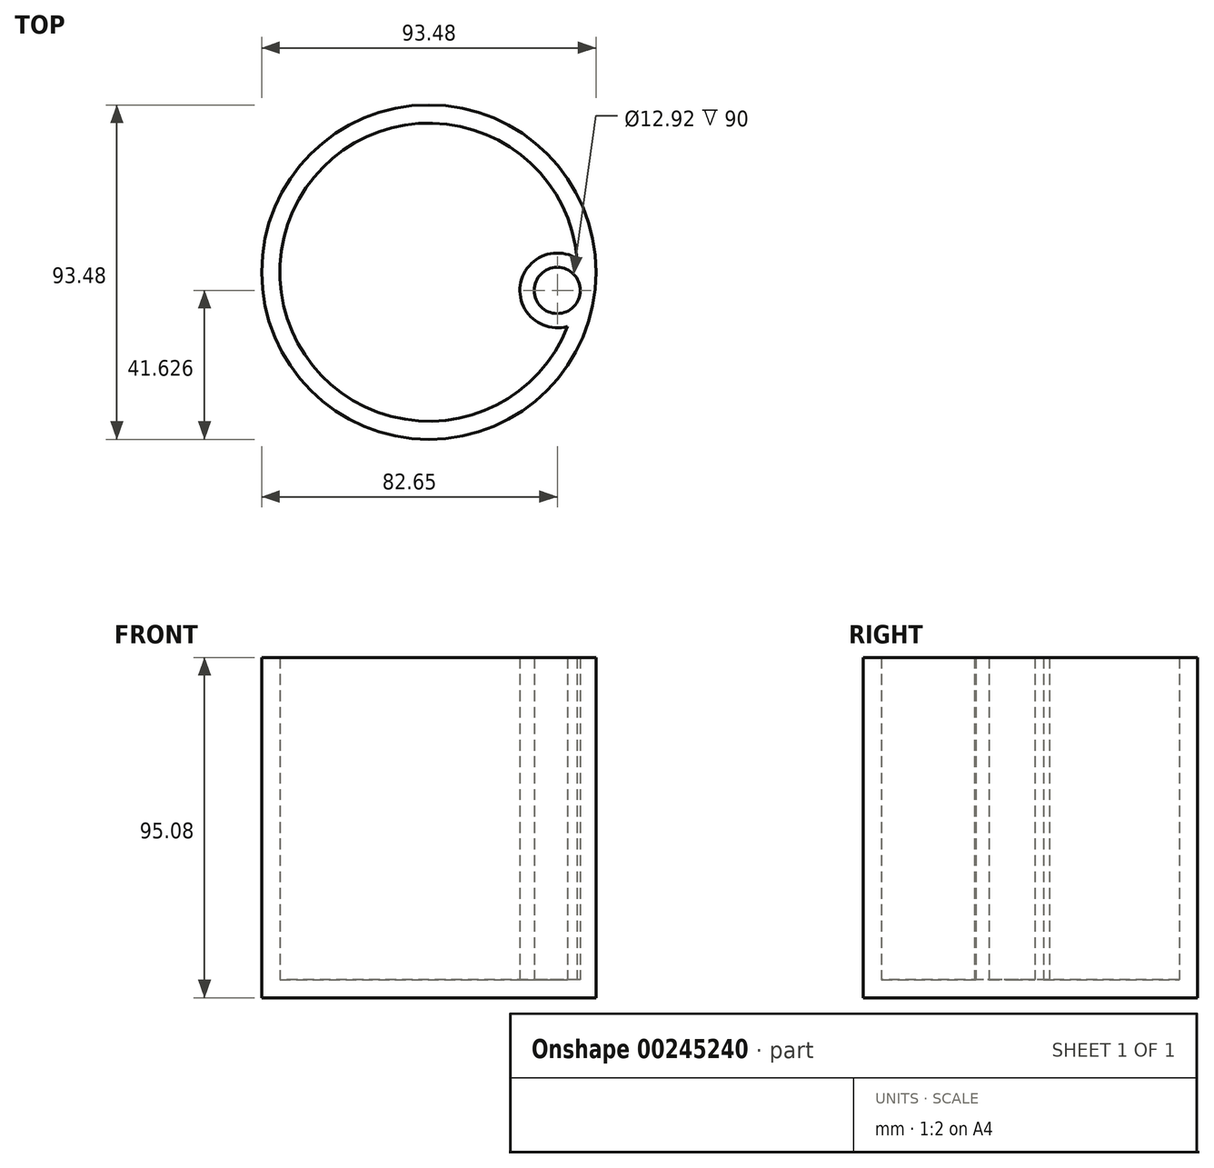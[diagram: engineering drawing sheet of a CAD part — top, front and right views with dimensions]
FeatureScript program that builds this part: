
annotation { "Feature Type Name" : "Feature", "Feature Type Description" : "" }
export const myFeature = defineFeature(function(context is Context, id is Id, definition is map)
    precondition{}
    {
        {
            var Q0;
            Q0=qCreatedBy(makeId("Top.planeOp"),FACE);
            var sketch = newSketch(context, id + "F0", { "sketchPlane" : qUnion([Q0])});
            skCircle(sketch, "E0", {"center": v(0, 0) * mm, "radius": 46.74 * mm});
            skCircle(sketch, "E1", {"center": v(35.9, -5.11) * mm, "radius": 10.46 * mm});
            skCircle(sketch, "E2", {"center": v(35.9, -5.11) * mm, "radius": 6.46 * mm});
            skCircle(sketch, "E3", {"center": v(0, 0) * mm, "radius": 41.66 * mm});
            skSolve(sketch);
        }
        {
            var Q0;
            {var subQ0=sQuery(id+"F0.wireOp",EDGE,"E3");var subQ1=sQuery(id+"F0.wireOp",EDGE,"E1");var subQ2=makeQuery(id+"F0.imprint","INTERSECT",VERTEX,{"disambiguationData":[OD(0.0)],"derivedFrom":[subQ1,subQ0]});Q0=makeQuery(id+"F0.imprint","IMPRINT",FACE,{"disambiguationData":[TD([[makeQuery(id+"F0.imprint","IMPRINT",EDGE,{"disambiguationData":[TD([[subQ2,1.0]])],"derivedFrom":subQ1}),1.0]])]});}
            var Q1;
            {var subQ0=sQuery(id+"F0.wireOp",EDGE,"E3");var subQ1=sQuery(id+"F0.wireOp",EDGE,"E1");var subQ2=makeQuery(id+"F0.imprint","INTERSECT",VERTEX,{"disambiguationData":[OD(0.0)],"derivedFrom":[subQ1,subQ0]});Q1=makeQuery(id+"F0.imprint","IMPRINT",FACE,{"disambiguationData":[TD([[makeQuery(id+"F0.imprint","IMPRINT",EDGE,{"disambiguationData":[TD([[subQ2,-1.0]])],"derivedFrom":subQ1}),1.0]])]});}
            var Q2;
            Q2=makeQuery(id+"F0.imprint","IMPRINT",FACE,{"disambiguationData":[TD([[makeQuery(id+"F0.imprint","IMPRINT",EDGE,{"derivedFrom":sQuery(id+"F0.wireOp",EDGE,"E0")}),1.0]])]});
            extrude(context, id + "F1", {"entities" : qUnion([Q0, Q1, Q2]), "depth" : 90 * mm});
        }
        {
            var Q0;
            Q0 = qSketchRegion(id + "F0", true);
            var Q1;
            {var subQ0=sQuery(id+"F0.wireOp",EDGE,"E3");var subQ1=sQuery(id+"F0.wireOp",EDGE,"E2");var subQ2=makeQuery(id+"F0.imprint","INTERSECT",VERTEX,{"disambiguationData":[OD(0.0)],"derivedFrom":[subQ1,subQ0]});Q1=makeQuery(id+"F0.imprint","IMPRINT",FACE,{"disambiguationData":[TD([[makeQuery(id+"F0.imprint","IMPRINT",EDGE,{"disambiguationData":[TD([[subQ2,1.0]])],"derivedFrom":subQ1}),1.0]])]});}
            var Q2;
            {var subQ0=sQuery(id+"F0.wireOp",EDGE,"E3");var subQ1=sQuery(id+"F0.wireOp",EDGE,"E2");var subQ2=makeQuery(id+"F0.imprint","INTERSECT",VERTEX,{"disambiguationData":[OD(0.0)],"derivedFrom":[subQ1,subQ0]});Q2=makeQuery(id+"F0.imprint","IMPRINT",FACE,{"disambiguationData":[TD([[makeQuery(id+"F0.imprint","IMPRINT",EDGE,{"disambiguationData":[TD([[subQ2,-1.0]])],"derivedFrom":subQ1}),1.0]])]});}
            var Q3;
            {var subQ0=sQuery(id+"F0.wireOp",EDGE,"E3");var subQ1=sQuery(id+"F0.wireOp",EDGE,"E1");var subQ2=makeQuery(id+"F0.imprint","INTERSECT",VERTEX,{"disambiguationData":[OD(0.0)],"derivedFrom":[subQ1,subQ0]});Q3=makeQuery(id+"F0.imprint","IMPRINT",FACE,{"disambiguationData":[TD([[makeQuery(id+"F0.imprint","IMPRINT",EDGE,{"disambiguationData":[TD([[subQ2,1.0]])],"derivedFrom":subQ1}),-1.0]])]});}
            var Q4;
            {var subQ0=sQuery(id+"F0.wireOp",EDGE,"E3");var subQ1=sQuery(id+"F0.wireOp",EDGE,"E1");var subQ2=makeQuery(id+"F0.imprint","INTERSECT",VERTEX,{"disambiguationData":[OD(0.0)],"derivedFrom":[subQ1,subQ0]});Q4=makeQuery(id+"F0.imprint","IMPRINT",FACE,{"disambiguationData":[TD([[makeQuery(id+"F0.imprint","IMPRINT",EDGE,{"disambiguationData":[TD([[subQ2,1.0]])],"derivedFrom":subQ1}),1.0]])]});}
            var Q5;
            {var subQ0=sQuery(id+"F0.wireOp",EDGE,"E3");var subQ1=sQuery(id+"F0.wireOp",EDGE,"E1");var subQ2=makeQuery(id+"F0.imprint","INTERSECT",VERTEX,{"disambiguationData":[OD(0.0)],"derivedFrom":[subQ1,subQ0]});Q5=makeQuery(id+"F0.imprint","IMPRINT",FACE,{"disambiguationData":[TD([[makeQuery(id+"F0.imprint","IMPRINT",EDGE,{"disambiguationData":[TD([[subQ2,-1.0]])],"derivedFrom":subQ1}),1.0]])]});}
            extrude(context, id + "F2", {"entities" : qUnion([Q0, Q1, Q2, Q3, Q4, Q5]), "operationType" : NewBodyOperationType.ADD, "oppositeDirection" : true, "depth" : 5.08 * mm});
        }
    });
